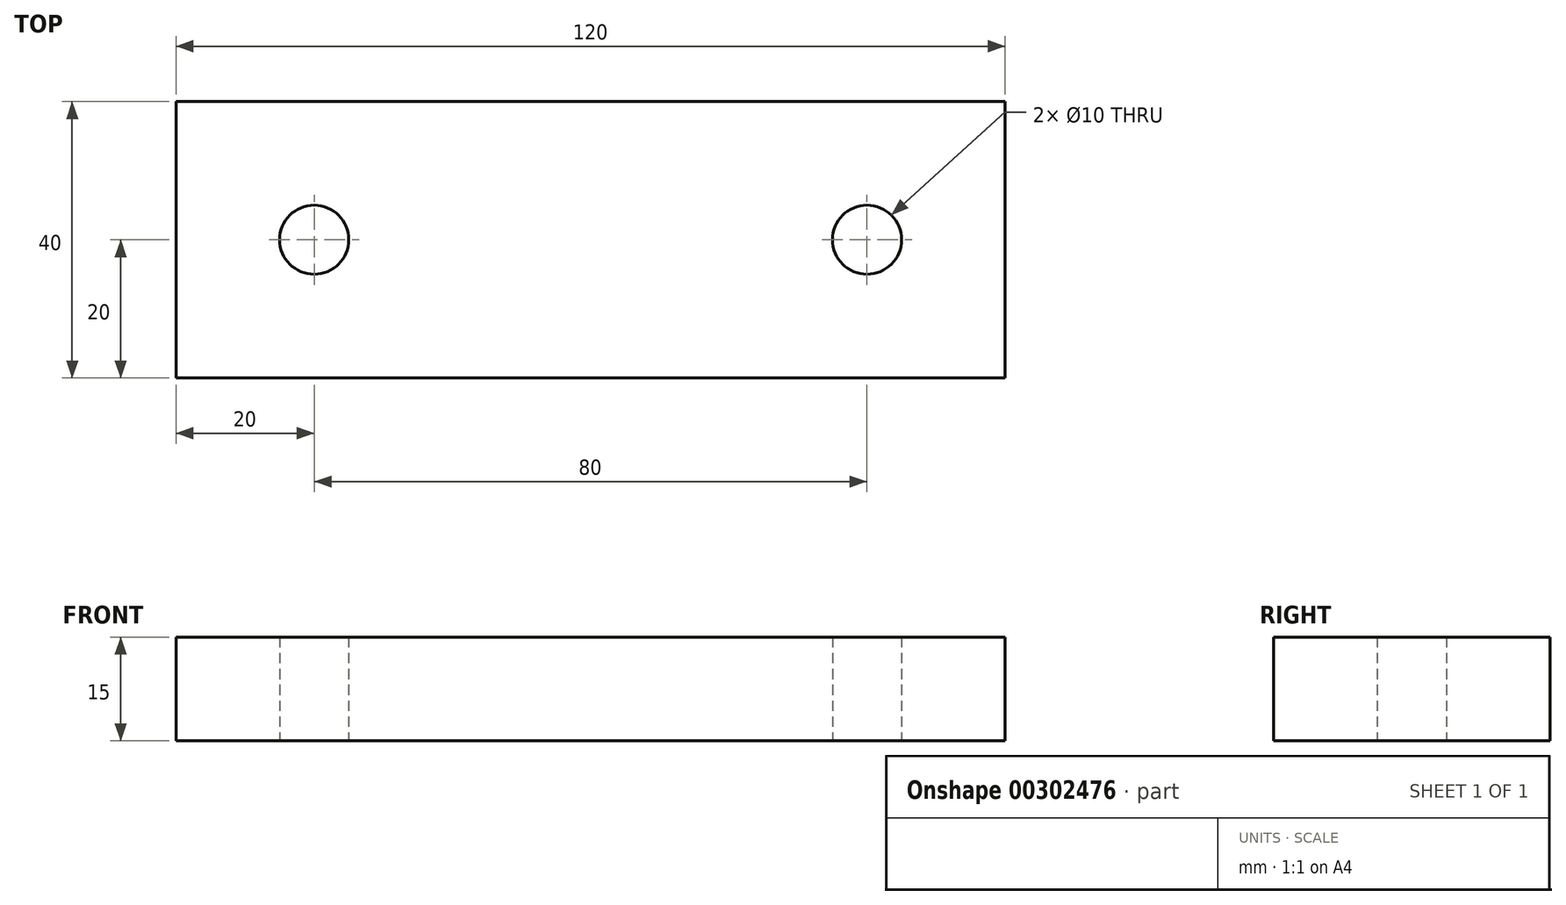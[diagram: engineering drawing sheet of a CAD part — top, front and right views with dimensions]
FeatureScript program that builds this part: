
annotation { "Feature Type Name" : "Feature", "Feature Type Description" : "" }
export const myFeature = defineFeature(function(context is Context, id is Id, definition is map)
    precondition{}
    {
        {
            var Q0;
            Q0=qCreatedBy(makeId("Top.planeOp"),FACE);
            var sketch = newSketch(context, id + "F0", { "sketchPlane" : qUnion([Q0])});
            skLineSegment(sketch, "E0", {"start": v(-60, 20) * mm, "end": v(60, 20) * mm});
            skLineSegment(sketch, "E1", {"start": v(60, 20) * mm, "end": v(60, -20) * mm});
            skLineSegment(sketch, "E2", {"start": v(60, -20) * mm, "end": v(-60, -20) * mm});
            skLineSegment(sketch, "E3", {"start": v(-60, -20) * mm, "end": v(-60, 20) * mm});
            skPoint(sketch, "E4", {"position": v(40, 0) * mm});
            skPoint(sketch, "E5", {"position": v(-40, 0) * mm});
            skCircle(sketch, "E6", {"center": v(-40, 0) * mm, "radius": 5 * mm});
            skCircle(sketch, "E7", {"center": v(40, 0) * mm, "radius": 5 * mm});
            skSolve(sketch);
        }
        {
            var Q0;
            Q0=makeQuery(id+"F0.imprint","IMPRINT",FACE,{"disambiguationData":[TD([[makeQuery(id+"F0.imprint","IMPRINT",EDGE,{"derivedFrom":sQuery(id+"F0.wireOp",EDGE,"E0")}),-1.0]])]});
            extrude(context, id + "F1", {"entities" : qUnion([Q0]), "depth" : 15 * mm});
        }
    });
